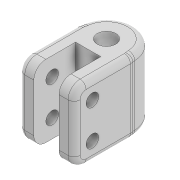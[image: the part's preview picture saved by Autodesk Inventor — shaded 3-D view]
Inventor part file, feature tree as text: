
AUTODESK INVENTOR PART (.ipt)
format: ipt  version: 2022 (Build 260153000, 153)  size: 216,064 bytes
history: native  units: mm
features: extrude x4, sketch x3, fillet x3
ambient origin geometry x8: Origin, YZ Plane, XZ Plane, XY Plane, X Axis, Y Axis, Z Axis, Center Point
bodies: Solid1 (feature_tree)
feature tree (10):
  extrude  "Extrusion1"  Depth=9.0mm
  sketch  "Sketch2"  dims[d2=12.0mm d3=0.0mm d4=4.2mm]
  extrude  "Extrusion2"  Depth=4.2mm
  extrude  "Extrusion4"  Depth=2.5mm
  extrude  "Extrusion3"  Depth=2.5mm
  fillet  "Fillet2"  Radius=10.0mm
  fillet  "Fillet3"  Radius=12.0mm
  fillet  "Fillet4"  Radius=2.1mm
  sketch  "Sketch1"  dims[d0=3.1mm d1=9.0mm]
  sketch  "Sketch3"  dims[d5=2.1mm d6=2.5mm d7=2.5mm d8=10.0mm d9=12.0mm d10=0.0mm d11=2.1mm d12=2.1mm d13=2.0mm d14=2.0mm d17=11.0mm d18=0.0mm d20=2.0mm d21=2.0mm d22=1.0mm d23=20.0mm d24=0.0mm d25=1.5mm d26=5.9mm d27=3.05mm]
